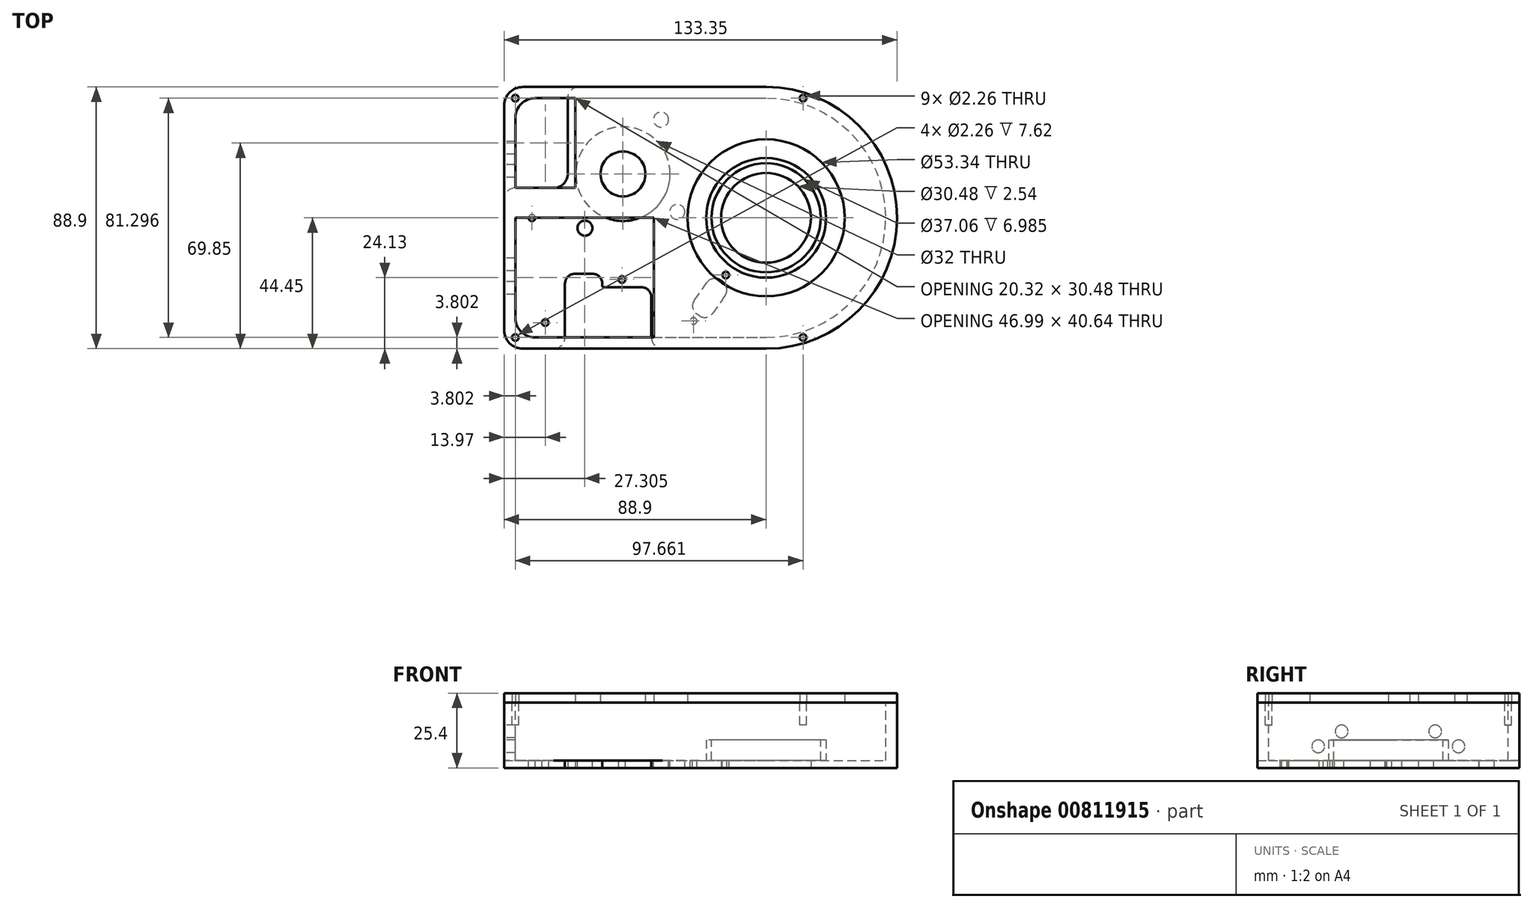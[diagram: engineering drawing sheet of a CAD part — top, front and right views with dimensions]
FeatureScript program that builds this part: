
annotation { "Feature Type Name" : "Feature", "Feature Type Description" : "" }
export const myFeature = defineFeature(function(context is Context, id is Id, definition is map)
    precondition{}
    {
        {
            var Q0;
            Q0=qCreatedBy(makeId("Top.planeOp"),FACE);
            var sketch = newSketch(context, id + "F0", { "sketchPlane" : qUnion([Q0])});
            skLineSegment(sketch, "E0.bottom", {"start": v(6.35, 0) * mm, "end": v(88.9, 0) * mm});
            skLineSegment(sketch, "E0.top", {"start": v(6.35, 88.9) * mm, "end": v(88.9, 88.9) * mm});
            skLineSegment(sketch, "E0.left", {"start": v(0, 6.35) * mm, "end": v(0, 82.55) * mm});
            skLineSegment(sketch, "E0.right", {"start": v(88.9, 0) * mm, "end": v(88.9, 88.9) * mm});
            skArc(sketch, "E1", {"start": v(88.9, 0) * mm, "mid": v(133.35, 44.45) * mm, "end": v(88.9, 88.9) * mm});
            skCircle(sketch, "E2", {"center": v(88.9, 44.45) * mm, "radius": 15.24 * mm});
            skPoint(sketch, "E3.visualSharp", {"position": v(0, 88.9) * mm});
            skArc(sketch, "E3.filletArc", {"start": v(6.35, 88.9) * mm, "mid": v(1.86, 87.04) * mm, "end": v(0, 82.55) * mm});
            skPoint(sketch, "E4.visualSharp", {"position": v(0, 0) * mm});
            skArc(sketch, "E4.filletArc", {"start": v(0, 6.35) * mm, "mid": v(1.86, 1.86) * mm, "end": v(6.35, 0) * mm});
            skSolve(sketch);
        }
        {
            var Q0;
            {var subQ4=sQuery(id+"F0.wireOp",EDGE,"E1");var subQ7=sQuery(id+"F0.wireOp",EDGE,"E0.bottom");Q0=qUnion([makeQuery(id+"F0.imprint","IMPRINT",FACE,{"disambiguationData":[TD([[makeQuery(id+"F0.imprint","IMPRINT",EDGE,{"derivedFrom":subQ7}),1.0]])]}),makeQuery(id+"F0.imprint","IMPRINT",FACE,{"disambiguationData":[TD([[makeQuery(id+"F0.imprint","IMPRINT",EDGE,{"derivedFrom":subQ4}),1.0]])]})]);}
            extrude(context, id + "F1", {"entities" : qUnion([Q0]), "depth" : 22.22 * mm});
        }
        {
            var Q0;
            Q0=makeQuery(id+"F1.opExtrude","CAP_FACE",FACE,{"disambiguationData":[OSD([sQuery(id+"F0.wireOp",EDGE,"E0.bottom"),sQuery(id+"F0.wireOp",EDGE,"E0.top"),sQuery(id+"F0.wireOp",EDGE,"E0.left"),sQuery(id+"F0.wireOp",EDGE,"E1"),sQuery(id+"F0.wireOp",EDGE,"E2")])],"isStart":false});
            var sketch = newSketch(context, id + "F2", { "sketchPlane" : qUnion([Q0])});
            skLineSegment(sketch, "E5.0", {"start": v(10.41, 85.1) * mm, "end": v(88.9, 85.1) * mm});
            skLineSegment(sketch, "E5.1", {"start": v(3.8, 10.41) * mm, "end": v(3.8, 78.49) * mm});
            skLineSegment(sketch, "E5.2", {"start": v(10.41, 3.8) * mm, "end": v(88.9, 3.8) * mm});
            skArc(sketch, "E5.3", {"start": v(88.9, 3.8) * mm, "mid": v(129.54, 44.45) * mm, "end": v(88.9, 85.1) * mm});
            skPoint(sketch, "E6.visualSharp", {"position": v(3.8, 85.1) * mm});
            skArc(sketch, "E6.filletArc", {"start": v(10.41, 85.1) * mm, "mid": v(5.74, 83.16) * mm, "end": v(3.8, 78.49) * mm});
            skPoint(sketch, "E7.visualSharp", {"position": v(3.8, 3.8) * mm});
            skArc(sketch, "E7.filletArc", {"start": v(3.8, 10.41) * mm, "mid": v(5.74, 5.74) * mm, "end": v(10.41, 3.8) * mm});
            skSolve(sketch);
        }
        {
            var Q0;
            {var subQ0=makeQuery(id+"F2.imprint","IMPRINT",EDGE,{"derivedFrom":makeQuery(id+"F1.opExtrude","CAP_EDGE",EDGE,{"disambiguationData":[OSD([sQuery(id+"F0.wireOp",EDGE,"E2")])],"isStart":false})});Q0=qUnion([makeQuery(id+"F2.imprint","IMPRINT",FACE,{"disambiguationData":[TD([[subQ0,1.0]])]}),makeQuery(id+"F2.imprint","IMPRINT",FACE,{"disambiguationData":[TD([[makeQuery(id+"F2.imprint","IMPRINT",EDGE,{"derivedFrom":sQuery(id+"F2.wireOp",EDGE,"E5.0")}),-1.0]])]})]);}
            extrude(context, id + "F3", {"entities" : qUnion([Q0]), "operationType" : NewBodyOperationType.REMOVE, "oppositeDirection" : true, "depth" : 19.68 * mm});
        }
        {
            var Q0;
            Q0=makeQuery(id+"F3.boolean.opBoolean","COPY",FACE,{"derivedFrom":makeQuery(id+"F3.opExtrude","CAP_FACE",FACE,{"disambiguationData":[OSD([sQuery(id+"F2.wireOp",EDGE,"E5.0"),sQuery(id+"F2.wireOp",EDGE,"E5.1"),sQuery(id+"F2.wireOp",EDGE,"E5.2"),sQuery(id+"F2.wireOp",EDGE,"E5.3"),sQuery(id+"F2.wireOp",EDGE,"E6.filletArc"),sQuery(id+"F2.wireOp",EDGE,"E7.filletArc")])],"isStart":false})});
            var sketch = newSketch(context, id + "F4", { "sketchPlane" : qUnion([Q0])});
            skArc(sketch, "E8.0", {"start": v(88.9, 3.8) * mm, "mid": v(129.54, 44.45) * mm, "end": v(88.9, 85.1) * mm, "construction": true});
            skCircle(sketch, "E9", {"center": v(88.9, 44.45) * mm, "radius": 20.32 * mm});
            skSolve(sketch);
        }
        {
            var Q0;
            {var subQ0=makeQuery(id+"F4.imprint","IMPRINT",EDGE,{"derivedFrom":makeQuery(id+"F3.boolean.opBoolean","INTERSECT",EDGE,{"derivedFrom":[makeQuery(id+"F1.opExtrude","SWEPT_FACE",FACE,{"disambiguationData":[OSD([sQuery(id+"F0.wireOp",EDGE,"E2")])]}),makeQuery(id+"F3.opExtrude","CAP_FACE",FACE,{"disambiguationData":[OSD([sQuery(id+"F2.wireOp",EDGE,"E5.0"),sQuery(id+"F2.wireOp",EDGE,"E5.1"),sQuery(id+"F2.wireOp",EDGE,"E5.2"),sQuery(id+"F2.wireOp",EDGE,"E5.3"),sQuery(id+"F2.wireOp",EDGE,"E6.filletArc"),sQuery(id+"F2.wireOp",EDGE,"E7.filletArc")])],"isStart":false})]})});Q0=qUnion([makeQuery(id+"F4.imprint","IMPRINT",FACE,{"disambiguationData":[TD([[subQ0,1.0]])]}),makeQuery(id+"F4.imprint","IMPRINT",FACE,{"disambiguationData":[TD([[makeQuery(id+"F4.imprint","IMPRINT",EDGE,{"derivedFrom":sQuery(id+"F4.wireOp",EDGE,"E9")}),1.0]])]})]);}
            extrude(context, id + "F5", {"entities" : qUnion([Q0]), "operationType" : NewBodyOperationType.ADD, "depth" : 7 * mm});
        }
        {
            var Q0;
            Q0=makeQuery(id+"F5.opExtrude","CAP_FACE",FACE,{"disambiguationData":[OSD([sQuery(id+"F4.wireOp",EDGE,"E9")])],"isStart":false});
            var sketch = newSketch(context, id + "F6", { "sketchPlane" : qUnion([Q0])});
            skCircle(sketch, "E10", {"center": v(88.9, 44.45) * mm, "radius": 18.53 * mm});
            skSolve(sketch);
        }
        {
            var Q0;
            Q0=makeQuery(id+"F6.imprint","IMPRINT",FACE,{"disambiguationData":[TD([[makeQuery(id+"F6.imprint","IMPRINT",EDGE,{"derivedFrom":sQuery(id+"F6.wireOp",EDGE,"E10")}),1.0]])]});
            extrude(context, id + "F7", {"entities" : qUnion([Q0]), "operationType" : NewBodyOperationType.REMOVE, "oppositeDirection" : true, "depth" : 7 * mm});
        }
        {
            var Q0;
            Q0=makeQuery(id+"F1.opExtrude","CAP_FACE",FACE,{"disambiguationData":[OSD([sQuery(id+"F0.wireOp",EDGE,"E0.bottom"),sQuery(id+"F0.wireOp",EDGE,"E0.top"),sQuery(id+"F0.wireOp",EDGE,"E0.left"),sQuery(id+"F0.wireOp",EDGE,"E1"),sQuery(id+"F0.wireOp",EDGE,"E2")])],"isStart":false});
            var sketch = newSketch(context, id + "F8", { "sketchPlane" : qUnion([Q0])});
            skLineSegment(sketch, "E11", {"start": v(101.46, 85.1) * mm, "end": v(101.46, 3.8) * mm, "construction": true});
            skCircle(sketch, "E12", {"center": v(101.46, 3.8) * mm, "radius": 1.13 * mm});
            skCircle(sketch, "E13", {"center": v(101.46, 85.1) * mm, "radius": 1.13 * mm});
            skCircle(sketch, "E14", {"center": v(3.8, 85.1) * mm, "radius": 1.13 * mm});
            skCircle(sketch, "E15", {"center": v(3.8, 3.8) * mm, "radius": 1.13 * mm});
            skLineSegment(sketch, "E16", {"start": v(1.86, 87.04) * mm, "end": v(5.74, 83.16) * mm, "construction": true});
            skLineSegment(sketch, "E17", {"start": v(1.86, 1.86) * mm, "end": v(5.74, 5.74) * mm, "construction": true});
            skLineSegment(sketch, "E18", {"start": v(3.8, 85.1) * mm, "end": v(101.46, 85.1) * mm, "construction": true});
            skLineSegment(sketch, "E19", {"start": v(3.8, 3.8) * mm, "end": v(101.46, 3.8) * mm, "construction": true});
            skSolve(sketch);
        }
        {
            var Q0;
            Q0=qSketchRegion(id+"F8",true);
            extrude(context, id + "F9", {"entities" : qUnion([Q0]), "operationType" : NewBodyOperationType.REMOVE, "oppositeDirection" : true, "depth" : 7.62 * mm});
        }
        {
            var Q0;
            Q0=makeQuery(id+"F3.boolean.opBoolean","COPY",FACE,{"derivedFrom":makeQuery(id+"F3.opExtrude","CAP_FACE",FACE,{"disambiguationData":[OSD([sQuery(id+"F2.wireOp",EDGE,"E5.0"),sQuery(id+"F2.wireOp",EDGE,"E5.1"),sQuery(id+"F2.wireOp",EDGE,"E5.2"),sQuery(id+"F2.wireOp",EDGE,"E5.3"),sQuery(id+"F2.wireOp",EDGE,"E6.filletArc"),sQuery(id+"F2.wireOp",EDGE,"E7.filletArc")])],"isStart":false})});
            var sketch = newSketch(context, id + "F10", { "sketchPlane" : qUnion([Q0])});
            skCircle(sketch, "E20", {"center": v(88.9, 44.45) * mm, "radius": 38.1 * mm, "construction": true});
            skCircle(sketch, "E21", {"center": v(40.34, 59.37) * mm, "radius": 12.7 * mm, "construction": true});
            skCircle(sketch, "E22", {"center": v(40.34, 59.37) * mm, "radius": 16 * mm});
            skCircle(sketch, "E23", {"center": v(40.34, 59.37) * mm, "radius": 22.5 * mm, "construction": true});
            skCircle(sketch, "E24", {"center": v(40.34, 59.37) * mm, "radius": 28.58 * mm, "construction": true});
            skLineSegment(sketch, "E25", {"start": v(21.91, 72.28) * mm, "end": v(58.77, 46.47) * mm, "construction": true});
            skLineSegment(sketch, "E26", {"start": v(27.43, 40.95) * mm, "end": v(53.25, 77.8) * mm, "construction": true});
            skCircle(sketch, "E27", {"center": v(53.25, 77.8) * mm, "radius": 2.55 * mm});
            skCircle(sketch, "E28", {"center": v(21.91, 72.28) * mm, "radius": 2.55 * mm, "construction": true});
            skCircle(sketch, "E29", {"center": v(27.43, 40.95) * mm, "radius": 2.55 * mm});
            skCircle(sketch, "E30", {"center": v(58.77, 46.47) * mm, "radius": 2.55 * mm});
            skLineSegment(sketch, "E31", {"start": v(88.9, 44.45) * mm, "end": v(61.6, 5.58) * mm, "construction": true});
            skCircle(sketch, "E32", {"center": v(75.25, 25.02) * mm, "radius": 1.13 * mm});
            skCircle(sketch, "E33", {"center": v(64.3, 9.43) * mm, "radius": 1.13 * mm});
            skLineSegment(sketch, "E34", {"start": v(60.1, 8.97) * mm, "end": v(74.26, 29.13) * mm, "construction": true});
            skLineSegment(sketch, "E35", {"start": v(74.26, 29.13) * mm, "end": v(79.45, 25.48) * mm, "construction": true});
            skLineSegment(sketch, "E36", {"start": v(79.45, 25.48) * mm, "end": v(65.29, 5.32) * mm, "construction": true});
            skLineSegment(sketch, "E37", {"start": v(65.29, 5.32) * mm, "end": v(60.1, 8.97) * mm, "construction": true});
            skLineSegment(sketch, "E38", {"start": v(72.37, 15.4) * mm, "end": v(67.17, 19.05) * mm, "construction": true});
            skLineSegment(sketch, "E39", {"start": v(64.54, 16.4) * mm, "end": v(68.77, 22.43) * mm});
            skLineSegment(sketch, "E40", {"start": v(73.37, 23.23) * mm, "end": v(74.2, 22.65) * mm});
            skLineSegment(sketch, "E41", {"start": v(75, 18.05) * mm, "end": v(70.77, 12.02) * mm});
            skLineSegment(sketch, "E42", {"start": v(66.17, 11.22) * mm, "end": v(65.34, 11.8) * mm});
            skPoint(sketch, "E43.visualSharp", {"position": v(70.67, 25.13) * mm});
            skArc(sketch, "E43.filletArc", {"start": v(73.37, 23.23) * mm, "mid": v(70.9, 23.78) * mm, "end": v(68.77, 22.43) * mm});
            skPoint(sketch, "E44.visualSharp", {"position": v(76.9, 20.75) * mm});
            skArc(sketch, "E44.filletArc", {"start": v(75, 18.05) * mm, "mid": v(75.56, 20.51) * mm, "end": v(74.2, 22.65) * mm});
            skPoint(sketch, "E45.visualSharp", {"position": v(68.87, 9.32) * mm});
            skArc(sketch, "E45.filletArc", {"start": v(66.17, 11.22) * mm, "mid": v(68.64, 10.66) * mm, "end": v(70.77, 12.02) * mm});
            skPoint(sketch, "E46.visualSharp", {"position": v(62.64, 13.7) * mm});
            skArc(sketch, "E46.filletArc", {"start": v(64.54, 16.4) * mm, "mid": v(63.99, 13.93) * mm, "end": v(65.34, 11.8) * mm});
            skSolve(sketch);
        }
        {
            var Q0;
            Q0=qSketchRegion(id+"F10",true);
            extrude(context, id + "F11", {"entities" : qUnion([Q0]), "operationType" : NewBodyOperationType.REMOVE, "oppositeDirection" : true, "depth" : 25.4 * mm});
        }
        {
            var Q0;
            Q0=makeQuery(id+"F1.opExtrude","CAP_FACE",FACE,{"disambiguationData":[OSD([sQuery(id+"F0.wireOp",EDGE,"E0.bottom"),sQuery(id+"F0.wireOp",EDGE,"E0.top"),sQuery(id+"F0.wireOp",EDGE,"E0.left"),sQuery(id+"F0.wireOp",EDGE,"E1"),sQuery(id+"F0.wireOp",EDGE,"E2")])],"isStart":false});
            var sketch = newSketch(context, id + "F12", { "sketchPlane" : qUnion([Q0])});
            skLineSegment(sketch, "E47.0", {"start": v(6.35, 88.9) * mm, "end": v(88.9, 88.9) * mm});
            skArc(sketch, "E48.0", {"start": v(88.9, 0) * mm, "mid": v(133.35, 44.45) * mm, "end": v(88.9, 88.9) * mm});
            skLineSegment(sketch, "E49.0", {"start": v(6.35, 0) * mm, "end": v(88.9, 0) * mm});
            skArc(sketch, "E50.0", {"start": v(0, 6.35) * mm, "mid": v(1.86, 1.86) * mm, "end": v(6.35, 0) * mm});
            skLineSegment(sketch, "E51.0", {"start": v(0, 6.35) * mm, "end": v(0, 82.55) * mm});
            skArc(sketch, "E52.0", {"start": v(6.35, 88.9) * mm, "mid": v(1.86, 87.04) * mm, "end": v(0, 82.55) * mm});
            skCircle(sketch, "E53.0", {"center": v(3.8, 85.1) * mm, "radius": 1.13 * mm});
            skCircle(sketch, "E54.0", {"center": v(101.46, 85.1) * mm, "radius": 1.13 * mm});
            skLineSegment(sketch, "E55.0.3", {"start": v(88.9, 88.9) * mm, "end": v(6.35, 88.9) * mm});
            skLineSegment(sketch, "E55.0.5", {"start": v(0, 82.55) * mm, "end": v(0, 6.35) * mm});
            skCircle(sketch, "E56.0", {"center": v(101.46, 3.8) * mm, "radius": 1.13 * mm});
            skCircle(sketch, "E57.0", {"center": v(3.8, 3.8) * mm, "radius": 1.13 * mm});
            skCircle(sketch, "E58", {"center": v(88.9, 44.45) * mm, "radius": 26.67 * mm});
            skCircle(sketch, "E59", {"center": v(40.34, 59.37) * mm, "radius": 7.62 * mm});
            skLineSegment(sketch, "E60.0", {"start": v(10.41, 3.8) * mm, "end": v(88.9, 3.8) * mm});
            skArc(sketch, "E61.0", {"start": v(3.8, 10.41) * mm, "mid": v(5.74, 5.74) * mm, "end": v(10.41, 3.8) * mm});
            skLineSegment(sketch, "E62.0", {"start": v(3.8, 10.41) * mm, "end": v(3.8, 78.49) * mm});
            skArc(sketch, "E63.0", {"start": v(10.41, 85.1) * mm, "mid": v(5.74, 83.16) * mm, "end": v(3.8, 78.49) * mm});
            skLineSegment(sketch, "E64.0", {"start": v(10.41, 85.1) * mm, "end": v(88.9, 85.1) * mm});
            skLineSegment(sketch, "E65", {"start": v(3.8, 44.45) * mm, "end": v(50.8, 44.45) * mm});
            skLineSegment(sketch, "E66", {"start": v(50.8, 44.45) * mm, "end": v(50.8, 3.8) * mm});
            skCircle(sketch, "E67", {"center": v(88.9, 44.45) * mm, "radius": 38.1 * mm, "construction": true});
            skLineSegment(sketch, "E68", {"start": v(3.8, 54.61) * mm, "end": v(24.13, 54.61) * mm});
            skLineSegment(sketch, "E69", {"start": v(24.13, 54.61) * mm, "end": v(24.13, 85.1) * mm});
            skSolve(sketch);
        }
        {
            var Q0;
            Q0=qSketchRegion(id+"F12",true);
            extrude(context, id + "F13", {"entities" : qUnion([Q0]), "depth" : 3.17 * mm});
        }
        {
            var Q0;
            Q0=makeQuery(id+"F1.opExtrude","SWEPT_FACE",FACE,{"disambiguationData":[OSD([sQuery(id+"F0.wireOp",EDGE,"E0.left")])]});
            var sketch = newSketch(context, id + "F14", { "sketchPlane" : qUnion([Q0])});
            skCircle(sketch, "E70", {"center": v(-68.26, 7.3) * mm, "radius": 2.16 * mm});
            skCircle(sketch, "E71", {"center": v(-20.64, 7.3) * mm, "radius": 2.16 * mm});
            skCircle(sketch, "E72", {"center": v(-60.33, 12.38) * mm, "radius": 2.16 * mm});
            skCircle(sketch, "E73", {"center": v(-28.58, 12.38) * mm, "radius": 2.16 * mm});
            skSolve(sketch);
        }
        {
            var Q0;
            {Q0=qUnion([makeQuery(id+"F14.imprint","IMPRINT",FACE,{"disambiguationData":[TD([[makeQuery(id+"F14.imprint","IMPRINT",EDGE,{"derivedFrom":sQuery(id+"F14.wireOp",EDGE,"E70")}),1.0]])]}),makeQuery(id+"F14.imprint","IMPRINT",FACE,{"disambiguationData":[TD([[makeQuery(id+"F14.imprint","IMPRINT",EDGE,{"derivedFrom":sQuery(id+"F14.wireOp",EDGE,"E71")}),1.0]])]}),makeQuery(id+"F14.imprint","IMPRINT",FACE,{"disambiguationData":[TD([[makeQuery(id+"F14.imprint","IMPRINT",EDGE,{"derivedFrom":sQuery(id+"F14.wireOp",EDGE,"E72")}),1.0]])]}),makeQuery(id+"F14.imprint","IMPRINT",FACE,{"disambiguationData":[TD([[makeQuery(id+"F14.imprint","IMPRINT",EDGE,{"derivedFrom":sQuery(id+"F14.wireOp",EDGE,"E73")}),1.0]])]})]);}
            var Q1;
            Q1=makeQuery(id+"F3.boolean.opBoolean","COPY",FACE,{"derivedFrom":makeQuery(id+"F3.opExtrude","SWEPT_FACE",FACE,{"disambiguationData":[OSD([sQuery(id+"F2.wireOp",EDGE,"E5.1")])]})});
            extrude(context, id + "F15", {"entities" : qUnion([Q0]), "operationType" : NewBodyOperationType.REMOVE, "endBound" : BoundingType.UP_TO_SURFACE, "oppositeDirection" : true, "endBoundEntityFace" : qUnion([Q1]), "depth" : 25.4 * mm});
        }
        {
            var Q0;
            Q0=makeQuery(id+"F1.opExtrude","CAP_FACE",FACE,{"disambiguationData":[OSD([sQuery(id+"F0.wireOp",EDGE,"E0.bottom"),sQuery(id+"F0.wireOp",EDGE,"E0.top"),sQuery(id+"F0.wireOp",EDGE,"E0.left"),sQuery(id+"F0.wireOp",EDGE,"E1"),sQuery(id+"F0.wireOp",EDGE,"E2")])],"isStart":true});
            var sketch = newSketch(context, id + "F16", { "sketchPlane" : qUnion([Q0])});
            skCircle(sketch, "E74", {"center": v(88.9, -44.45) * mm, "radius": 28.57 * mm, "construction": true});
            skLineSegment(sketch, "E75.bottom", {"start": v(60.32, -73.03) * mm, "end": v(117.47, -73.03) * mm, "construction": true});
            skLineSegment(sketch, "E75.top", {"start": v(60.32, -15.88) * mm, "end": v(117.47, -15.88) * mm, "construction": true});
            skLineSegment(sketch, "E75.left", {"start": v(60.32, -73.03) * mm, "end": v(60.32, -15.88) * mm, "construction": true});
            skLineSegment(sketch, "E75.right", {"start": v(117.47, -73.03) * mm, "end": v(117.47, -15.88) * mm, "construction": true});
            skCircle(sketch, "E76", {"center": v(65.09, -68.26) * mm, "radius": 2.16 * mm});
            skCircle(sketch, "E77", {"center": v(65.09, -20.64) * mm, "radius": 2.16 * mm});
            skSolve(sketch);
        }
        {
            var Q0;
            Q0=makeQuery(id+"F3.boolean.opBoolean","COPY",FACE,{"derivedFrom":makeQuery(id+"F3.opExtrude","CAP_FACE",FACE,{"disambiguationData":[OSD([sQuery(id+"F2.wireOp",EDGE,"E5.0"),sQuery(id+"F2.wireOp",EDGE,"E5.1"),sQuery(id+"F2.wireOp",EDGE,"E5.2"),sQuery(id+"F2.wireOp",EDGE,"E5.3"),sQuery(id+"F2.wireOp",EDGE,"E6.filletArc"),sQuery(id+"F2.wireOp",EDGE,"E7.filletArc")])],"isStart":false})});
            var sketch = newSketch(context, id + "F17", { "sketchPlane" : qUnion([Q0])});
            skCircle(sketch, "E78", {"center": v(9.45, 44.45) * mm, "radius": 1.13 * mm});
            skCircle(sketch, "E79.cCircle", {"center": v(9.45, 44.45) * mm, "radius": 3.67 * mm, "construction": true});
            skLineSegment(sketch, "E79.0", {"start": v(12.07, 41.89) * mm, "end": v(8.54, 40.9) * mm, "construction": true});
            skLineSegment(sketch, "E79.1", {"start": v(8.54, 40.9) * mm, "end": v(5.92, 43.46) * mm, "construction": true});
            skLineSegment(sketch, "E79.2", {"start": v(5.92, 43.46) * mm, "end": v(6.83, 47.01) * mm, "construction": true});
            skLineSegment(sketch, "E79.3", {"start": v(6.83, 47.01) * mm, "end": v(10.36, 48) * mm, "construction": true});
            skLineSegment(sketch, "E79.4", {"start": v(10.36, 48) * mm, "end": v(12.98, 45.44) * mm, "construction": true});
            skLineSegment(sketch, "E79.5", {"start": v(12.98, 45.44) * mm, "end": v(12.07, 41.89) * mm, "construction": true});
            skCircle(sketch, "E80", {"center": v(13.96, 8.86) * mm, "radius": 1.13 * mm});
            skCircle(sketch, "E81", {"center": v(40, 23.48) * mm, "radius": 1.13 * mm});
            skSolve(sketch);
        }
        {
            var Q0;
            Q0=qSketchRegion(id+"F17",true);
            extrude(context, id + "F18", {"entities" : qUnion([Q0]), "operationType" : NewBodyOperationType.REMOVE, "endBound" : BoundingType.THROUGH_ALL, "oppositeDirection" : true, "depth" : 25.4 * mm});
        }
        {
            var Q0;
            Q0=makeQuery(id+"F1.opExtrude","CAP_FACE",FACE,{"disambiguationData":[OSD([sQuery(id+"F0.wireOp",EDGE,"E0.bottom"),sQuery(id+"F0.wireOp",EDGE,"E0.top"),sQuery(id+"F0.wireOp",EDGE,"E0.left"),sQuery(id+"F0.wireOp",EDGE,"E1"),sQuery(id+"F0.wireOp",EDGE,"E2"),sQuery(id+"F0.wireOp",EDGE,"E3.filletArc"),sQuery(id+"F0.wireOp",EDGE,"E4.filletArc")])],"isStart":true});
            var sketch = newSketch(context, id + "F19", { "sketchPlane" : qUnion([Q0])});
            skLineSegment(sketch, "E82.top", {"start": v(16.76, -54.61) * mm, "end": v(3.8, -54.61) * mm});
            skLineSegment(sketch, "E82.left", {"start": v(21.59, -85.1) * mm, "end": v(21.59, -59.44) * mm});
            skLineSegment(sketch, "E83.0", {"start": v(21.59, -85.1) * mm, "end": v(88.9, -85.1) * mm, "construction": true});
            skLineSegment(sketch, "E84.0", {"start": v(10.41, -3.8) * mm, "end": v(88.9, -3.8) * mm, "construction": true});
            skLineSegment(sketch, "E85.0", {"start": v(3.8, -10.41) * mm, "end": v(3.8, -54.61) * mm, "construction": true});
            skLineSegment(sketch, "E86", {"start": v(25.4, -88.9) * mm, "end": v(25.4, -88.9) * mm});
            skLineSegment(sketch, "E87", {"start": v(0, -50.8) * mm, "end": v(0, -50.8) * mm});
            skLineSegment(sketch, "E88", {"start": v(21.59, -85.1) * mm, "end": v(21.59, -85.1) * mm});
            skLineSegment(sketch, "E89", {"start": v(3.8, -54.61) * mm, "end": v(3.81, -54.61) * mm});
            skPoint(sketch, "E90.orphan", {"position": v(3.8, -78.49) * mm});
            skLineSegment(sketch, "E91.0", {"start": v(0, -50.8) * mm, "end": v(0, -82.55) * mm});
            skArc(sketch, "E92.0", {"start": v(6.35, -88.9) * mm, "mid": v(1.86, -87.04) * mm, "end": v(0, -82.55) * mm});
            skLineSegment(sketch, "E93.0", {"start": v(6.35, -88.9) * mm, "end": v(25.4, -88.9) * mm});
            skPoint(sketch, "E94.orphan", {"position": v(0, -6.35) * mm});
            skPoint(sketch, "E95.orphan", {"position": v(88.9, -88.9) * mm});
            skPoint(sketch, "E82.bottom.end.orphan", {"position": v(10.41, -85.1) * mm});
            skPoint(sketch, "E96.visualSharp", {"position": v(0, -54.61) * mm});
            skArc(sketch, "E96.filletArc", {"start": v(0, -50.8) * mm, "mid": v(1.12, -53.5) * mm, "end": v(3.81, -54.61) * mm});
            skPoint(sketch, "E97.visualSharp", {"position": v(21.59, -88.9) * mm});
            skArc(sketch, "E97.filletArc", {"start": v(21.59, -85.1) * mm, "mid": v(22.7, -87.78) * mm, "end": v(25.4, -88.9) * mm});
            skPoint(sketch, "E98.visualSharp", {"position": v(21.59, -54.61) * mm});
            skArc(sketch, "E98.filletArc", {"start": v(21.59, -59.44) * mm, "mid": v(20.18, -56.02) * mm, "end": v(16.76, -54.61) * mm});
            skLineSegment(sketch, "E99.bottom", {"start": v(20.65, 0) * mm, "end": v(49.99, 0) * mm});
            skLineSegment(sketch, "E99.top", {"start": v(33.86, -20.83) * mm, "end": v(46.69, -20.83) * mm});
            skLineSegment(sketch, "E99.left", {"start": v(20.65, -3.8) * mm, "end": v(20.65, -20.83) * mm});
            skLineSegment(sketch, "E99.right", {"start": v(49.99, -3.81) * mm, "end": v(49.99, -17.53) * mm});
            skLineSegment(sketch, "E100.top", {"start": v(23.95, -25.4) * mm, "end": v(30.05, -25.4) * mm});
            skLineSegment(sketch, "E100.left", {"start": v(20.65, -20.83) * mm, "end": v(20.65, -22.1) * mm});
            skLineSegment(sketch, "E100.right", {"start": v(33.35, -21.34) * mm, "end": v(33.35, -22.1) * mm});
            skPoint(sketch, "E101.visualSharp", {"position": v(20.65, -25.4) * mm});
            skArc(sketch, "E101.filletArc", {"start": v(20.65, -22.1) * mm, "mid": v(21.62, -24.43) * mm, "end": v(23.95, -25.4) * mm});
            skPoint(sketch, "E102.visualSharp", {"position": v(33.35, -25.4) * mm});
            skArc(sketch, "E102.filletArc", {"start": v(30.05, -25.4) * mm, "mid": v(32.38, -24.43) * mm, "end": v(33.35, -22.1) * mm});
            skLineSegment(sketch, "E103", {"start": v(16.84, 0) * mm, "end": v(16.84, 0) * mm});
            skLineSegment(sketch, "E104", {"start": v(53.8, 0) * mm, "end": v(53.8, 0) * mm});
            skPoint(sketch, "E105.visualSharp", {"position": v(20.65, 0) * mm});
            skArc(sketch, "E105.filletArc", {"start": v(20.65, -3.8) * mm, "mid": v(19.53, -1.12) * mm, "end": v(16.84, 0) * mm});
            skPoint(sketch, "E106.visualSharp", {"position": v(49.99, 0) * mm});
            skArc(sketch, "E106.filletArc", {"start": v(53.8, 0) * mm, "mid": v(51.1, -1.12) * mm, "end": v(49.99, -3.8) * mm});
            skLineSegment(sketch, "E107", {"start": v(16.84, 0) * mm, "end": v(53.8, 0) * mm});
            skPoint(sketch, "E108.visualSharp", {"position": v(33.35, -20.83) * mm});
            skArc(sketch, "E108.filletArc", {"start": v(33.86, -20.83) * mm, "mid": v(33.5, -20.98) * mm, "end": v(33.35, -21.34) * mm});
            skPoint(sketch, "E109.visualSharp", {"position": v(49.99, -20.83) * mm});
            skArc(sketch, "E109.filletArc", {"start": v(46.69, -20.83) * mm, "mid": v(49.02, -19.86) * mm, "end": v(49.99, -17.53) * mm});
            skSolve(sketch);
        }
        {
            var Q0;
            Q0=qSketchRegion(id+"F19",true);
            extrude(context, id + "F20", {"entities" : qUnion([Q0]), "operationType" : NewBodyOperationType.REMOVE, "oppositeDirection" : true, "depth" : 2.54 * mm});
        }
    });
